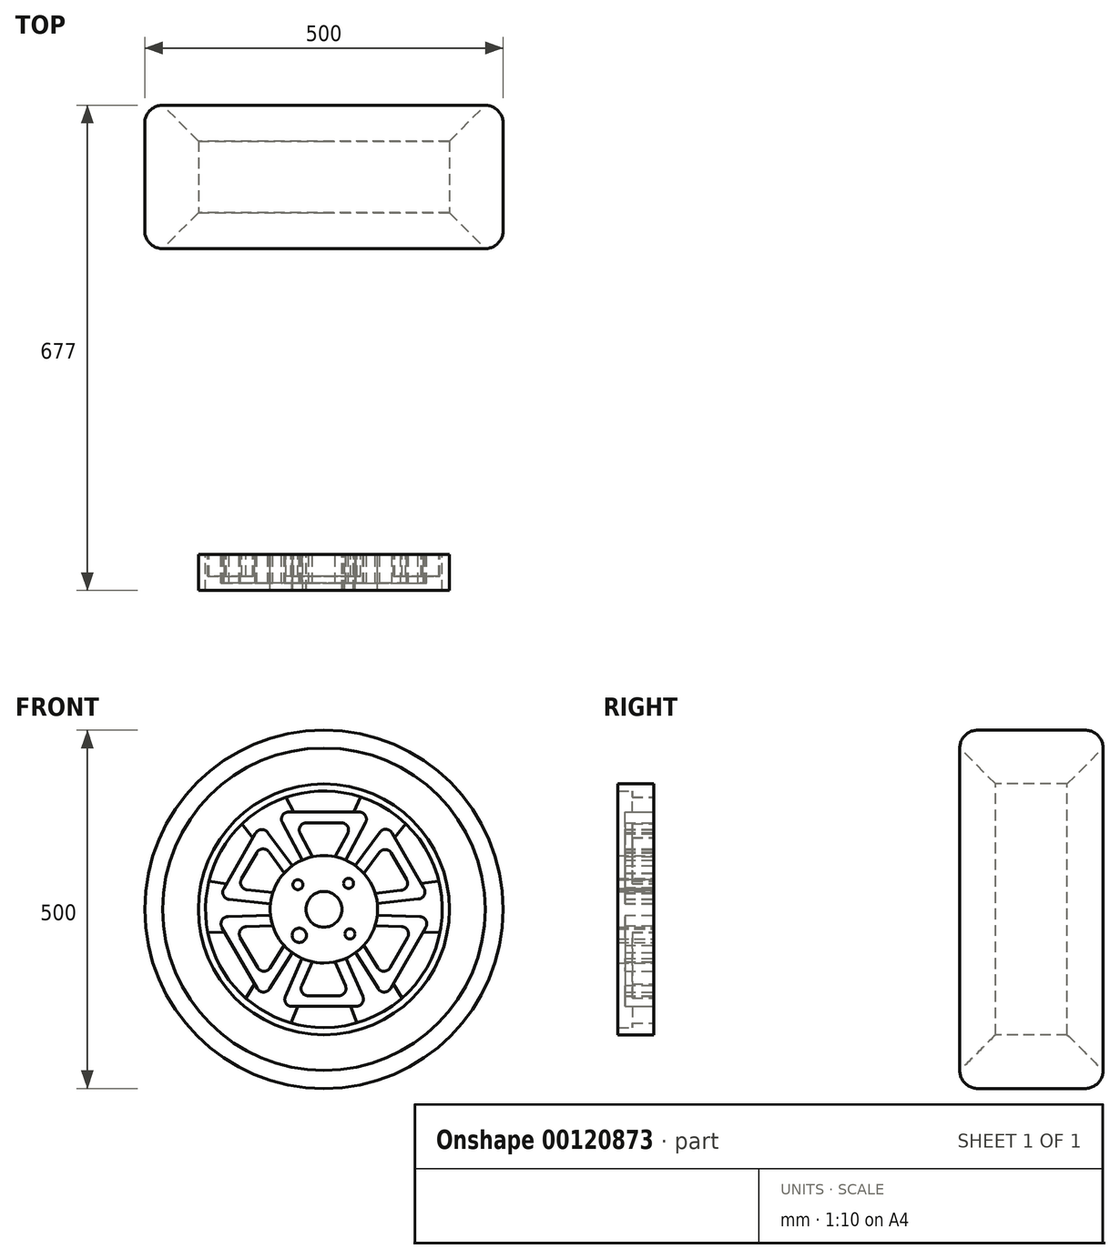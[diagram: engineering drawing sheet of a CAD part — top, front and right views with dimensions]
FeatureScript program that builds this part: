
annotation { "Feature Type Name" : "Feature", "Feature Type Description" : "" }
export const myFeature = defineFeature(function(context is Context, id is Id, definition is map)
    precondition{}
    {
        {
            var Q0;
            Q0=qCreatedBy(makeId("Front.planeOp"),FACE);
            var sketch = newSketch(context, id + "F0", { "sketchPlane" : qUnion([Q0])});
            skCircle(sketch, "E0", {"center": v(0, 0) * mm, "radius": 12.5 * mm});
            skCircle(sketch, "E1", {"center": v(0, 0) * mm, "radius": 25 * mm});
            skCircle(sketch, "E2", {"center": v(0, 0) * mm, "radius": 165.1 * mm});
            skCircle(sketch, "E3", {"center": v(0, 0) * mm, "radius": 175 * mm});
            skCircle(sketch, "E4", {"center": v(0, 0) * mm, "radius": 75 * mm});
            skLineSegment(sketch, "E5", {"start": v(0, 0) * mm, "end": v(0, 197.22) * mm, "construction": true});
            skLineSegment(sketch, "E6", {"start": v(-49.3, 135.7) * mm, "end": v(0, 135.7) * mm});
            skLineSegment(sketch, "E7.trimOffspring", {"start": v(-30.35, 68.58) * mm, "end": v(-58.13, 121.02) * mm});
            skLineSegment(sketch, "E8.MirrorCS", {"start": v(49.3, 135.7) * mm, "end": v(0, 135.7) * mm});
            skLineSegment(sketch, "E9.MirrorCS", {"start": v(30.35, 68.58) * mm, "end": v(58.13, 121.02) * mm});
            skLineSegment(sketch, "E10", {"start": v(-41.82, 135.7) * mm, "end": v(-52.8, 156.43) * mm});
            skLineSegment(sketch, "E11.MirrorCS", {"start": v(41.82, 135.7) * mm, "end": v(52.8, 156.43) * mm});
            skLineSegment(sketch, "E12.0", {"start": v(15.88, 73.3) * mm, "end": v(33.21, 106.02) * mm});
            skLineSegment(sketch, "E12.1", {"start": v(24.38, 120.7) * mm, "end": v(-1.73, 120.7) * mm});
            skLineSegment(sketch, "E12.2", {"start": v(-24.38, 120.7) * mm, "end": v(-1.73, 120.7) * mm});
            skLineSegment(sketch, "E12.3", {"start": v(-15.88, 73.3) * mm, "end": v(-33.21, 106.02) * mm});
            skPoint(sketch, "E13.visualSharp", {"position": v(-41, 120.7) * mm});
            skArc(sketch, "E13.filletArc", {"start": v(-24.38, 120.7) * mm, "mid": v(-32.94, 115.86) * mm, "end": v(-33.21, 106.02) * mm});
            skPoint(sketch, "E14.visualSharp", {"position": v(41, 120.7) * mm});
            skArc(sketch, "E14.filletArc", {"start": v(33.21, 106.02) * mm, "mid": v(32.94, 115.86) * mm, "end": v(24.38, 120.7) * mm});
            skPoint(sketch, "E15.visualSharp", {"position": v(65.91, 135.7) * mm});
            skArc(sketch, "E15.filletArc", {"start": v(58.13, 121.02) * mm, "mid": v(57.87, 130.86) * mm, "end": v(49.3, 135.7) * mm});
            skPoint(sketch, "E16.visualSharp", {"position": v(-65.91, 135.7) * mm});
            skArc(sketch, "E16.filletArc", {"start": v(-49.3, 135.7) * mm, "mid": v(-57.87, 130.86) * mm, "end": v(-58.13, 121.02) * mm});
            skLineSegment(sketch, "E17.1.0", {"start": v(-142.17, -25.16) * mm, "end": v(-117.52, -67.85) * mm});
            skLineSegment(sketch, "E17.1.1", {"start": v(-92.87, -110.54) * mm, "end": v(-117.52, -67.85) * mm});
            skArc(sketch, "E17.1.2", {"start": v(-92.87, -110.54) * mm, "mid": v(-84.4, -115.54) * mm, "end": v(-75.74, -110.86) * mm});
            skLineSegment(sketch, "E17.1.3", {"start": v(-44.22, -60.58) * mm, "end": v(-75.74, -110.86) * mm});
            skLineSegment(sketch, "E17.1.4", {"start": v(-55.54, -50.4) * mm, "end": v(-75.21, -81.77) * mm});
            skArc(sketch, "E17.1.5", {"start": v(-92.34, -81.46) * mm, "mid": v(-83.87, -86.46) * mm, "end": v(-75.21, -81.77) * mm});
            skLineSegment(sketch, "E17.1.6", {"start": v(-92.34, -81.46) * mm, "end": v(-103.67, -61.85) * mm});
            skLineSegment(sketch, "E17.1.7", {"start": v(-116.72, -39.24) * mm, "end": v(-103.67, -61.85) * mm});
            skArc(sketch, "E17.1.8", {"start": v(-108.42, -24.25) * mm, "mid": v(-116.8, -29.4) * mm, "end": v(-116.72, -39.24) * mm});
            skLineSegment(sketch, "E17.1.9", {"start": v(-71.42, -22.9) * mm, "end": v(-108.42, -24.25) * mm});
            skLineSegment(sketch, "E17.1.10", {"start": v(-74.57, -8) * mm, "end": v(-133.88, -10.17) * mm});
            skArc(sketch, "E17.1.11", {"start": v(-133.88, -10.17) * mm, "mid": v(-142.26, -15.32) * mm, "end": v(-142.17, -25.16) * mm});
            skLineSegment(sketch, "E17.2.0", {"start": v(92.87, -110.54) * mm, "end": v(117.52, -67.85) * mm});
            skLineSegment(sketch, "E17.2.1", {"start": v(142.17, -25.16) * mm, "end": v(117.52, -67.85) * mm});
            skArc(sketch, "E17.2.2", {"start": v(142.17, -25.16) * mm, "mid": v(142.26, -15.32) * mm, "end": v(133.88, -10.17) * mm});
            skLineSegment(sketch, "E17.2.3", {"start": v(74.57, -8) * mm, "end": v(133.88, -10.17) * mm});
            skLineSegment(sketch, "E17.2.4", {"start": v(71.42, -22.9) * mm, "end": v(108.42, -24.25) * mm});
            skArc(sketch, "E17.2.5", {"start": v(116.72, -39.24) * mm, "mid": v(116.8, -29.4) * mm, "end": v(108.42, -24.25) * mm});
            skLineSegment(sketch, "E17.2.6", {"start": v(116.72, -39.24) * mm, "end": v(105.4, -58.85) * mm});
            skLineSegment(sketch, "E17.2.7", {"start": v(92.34, -81.46) * mm, "end": v(105.4, -58.85) * mm});
            skArc(sketch, "E17.2.8", {"start": v(75.21, -81.77) * mm, "mid": v(83.87, -86.46) * mm, "end": v(92.34, -81.46) * mm});
            skLineSegment(sketch, "E17.2.9", {"start": v(55.54, -50.4) * mm, "end": v(75.21, -81.77) * mm});
            skLineSegment(sketch, "E17.2.10", {"start": v(44.22, -60.58) * mm, "end": v(75.74, -110.86) * mm});
            skArc(sketch, "E17.2.11", {"start": v(75.74, -110.86) * mm, "mid": v(84.4, -115.54) * mm, "end": v(92.87, -110.54) * mm});
            skLineSegment(sketch, "E18.1.0", {"start": v(138.43, -31.64) * mm, "end": v(161.87, -32.5) * mm});
            skLineSegment(sketch, "E18.1.1", {"start": v(96.61, -104.07) * mm, "end": v(109.07, -123.94) * mm});
            skLineSegment(sketch, "E18.2.0", {"start": v(-96.61, -104.07) * mm, "end": v(-109.07, -123.94) * mm});
            skLineSegment(sketch, "E18.2.1", {"start": v(-138.43, -31.64) * mm, "end": v(-161.87, -32.5) * mm});
            skLineSegment(sketch, "E19.MirrorCS", {"start": v(95.06, 106.32) * mm, "end": v(116.88, 68.53) * mm});
            skLineSegment(sketch, "E20.MirrorCS", {"start": v(94.06, 78.37) * mm, "end": v(104.71, 59.92) * mm});
            skLineSegment(sketch, "E21.MirrorCS", {"start": v(55.86, 50.05) * mm, "end": v(77.34, 79.3) * mm});
            skLineSegment(sketch, "E22.MirrorCS", {"start": v(43.77, 60.9) * mm, "end": v(78.05, 107.56) * mm});
            skArc(sketch, "E23.MirrorCS", {"start": v(77.34, 79.3) * mm, "mid": v(85.95, 83.36) * mm, "end": v(94.06, 78.37) * mm});
            skArc(sketch, "E24.MirrorCS", {"start": v(78.05, 107.56) * mm, "mid": v(86.9, 111.7) * mm, "end": v(95.06, 106.32) * mm});
            skLineSegment(sketch, "E25.MirrorCS", {"start": v(138.88, 30.41) * mm, "end": v(116.88, 68.53) * mm});
            skLineSegment(sketch, "E26.MirrorCS", {"start": v(115.14, 41.86) * mm, "end": v(104.71, 59.92) * mm});
            skArc(sketch, "E27.MirrorCS", {"start": v(107.28, 26.4) * mm, "mid": v(115.68, 31.85) * mm, "end": v(115.14, 41.86) * mm});
            skLineSegment(sketch, "E28.MirrorCS", {"start": v(71.56, 22.46) * mm, "end": v(107.28, 26.4) * mm});
            skLineSegment(sketch, "E29.MirrorCS", {"start": v(74.58, 7.95) * mm, "end": v(131.54, 14.24) * mm});
            skArc(sketch, "E30.MirrorCS", {"start": v(131.54, 14.24) * mm, "mid": v(140.13, 20.1) * mm, "end": v(138.88, 30.41) * mm});
            skLineSegment(sketch, "E31.MirrorCS", {"start": v(41.82, 135.7) * mm, "end": v(51.15, 156.98) * mm});
            skLineSegment(sketch, "E32", {"start": v(98.57, 100.23) * mm, "end": v(114.27, 119.17) * mm});
            skLineSegment(sketch, "E33.MirrorCS", {"start": v(135.6, 36.1) * mm, "end": v(160.3, 39.5) * mm});
            skLineSegment(sketch, "E34.1.0", {"start": v(-74.63, 7.46) * mm, "end": v(-132.17, 13.81) * mm});
            skLineSegment(sketch, "E34.1.1", {"start": v(-71.27, 23.35) * mm, "end": v(-107.34, 27.33) * mm});
            skArc(sketch, "E34.1.2", {"start": v(-107.34, 27.33) * mm, "mid": v(-115.16, 32.75) * mm, "end": v(-114.9, 42.27) * mm});
            skArc(sketch, "E34.1.3", {"start": v(-132.17, 13.81) * mm, "mid": v(-140.19, 19.4) * mm, "end": v(-139.6, 29.16) * mm});
            skLineSegment(sketch, "E34.1.4", {"start": v(-136.09, 35.25) * mm, "end": v(-160.34, 39.38) * mm});
            skLineSegment(sketch, "E34.1.5", {"start": v(-139.6, 29.16) * mm, "end": v(-117.78, 66.95) * mm});
            skLineSegment(sketch, "E34.1.6", {"start": v(-114.9, 42.27) * mm, "end": v(-104.25, 60.73) * mm});
            skLineSegment(sketch, "E34.1.7", {"start": v(-93.82, 78.79) * mm, "end": v(-104.25, 60.73) * mm});
            skArc(sketch, "E34.1.8", {"start": v(-76.5, 79.7) * mm, "mid": v(-85.43, 84.25) * mm, "end": v(-93.82, 78.79) * mm});
            skLineSegment(sketch, "E34.1.9", {"start": v(-55.23, 50.74) * mm, "end": v(-76.5, 79.7) * mm});
            skLineSegment(sketch, "E34.1.10", {"start": v(-95.78, 105.07) * mm, "end": v(-117.78, 66.95) * mm});
            skLineSegment(sketch, "E34.1.11", {"start": v(-44.17, 60.61) * mm, "end": v(-78.1, 106.8) * mm});
            skArc(sketch, "E34.1.12", {"start": v(-78.1, 106.8) * mm, "mid": v(-87.47, 111.31) * mm, "end": v(-95.78, 105.07) * mm});
            skLineSegment(sketch, "E34.1.13", {"start": v(-99.06, 99.39) * mm, "end": v(-114.35, 119.09) * mm});
            skLineSegment(sketch, "E34.2.0", {"start": v(30.86, -68.36) * mm, "end": v(54.12, -121.37) * mm});
            skLineSegment(sketch, "E34.2.1", {"start": v(15.42, -73.4) * mm, "end": v(30, -106.62) * mm});
            skArc(sketch, "E34.2.2", {"start": v(30, -106.62) * mm, "mid": v(29.22, -116.11) * mm, "end": v(20.84, -120.64) * mm});
            skArc(sketch, "E34.2.3", {"start": v(54.12, -121.37) * mm, "mid": v(53.29, -131.1) * mm, "end": v(44.55, -135.48) * mm});
            skLineSegment(sketch, "E34.2.4", {"start": v(37.51, -135.48) * mm, "end": v(46.07, -158.54) * mm});
            skLineSegment(sketch, "E34.2.5", {"start": v(44.55, -135.48) * mm, "end": v(0.9, -135.48) * mm});
            skLineSegment(sketch, "E34.2.6", {"start": v(20.84, -120.64) * mm, "end": v(-0.47, -120.64) * mm});
            skLineSegment(sketch, "E34.2.7", {"start": v(-21.32, -120.64) * mm, "end": v(-0.47, -120.64) * mm});
            skArc(sketch, "E34.2.8", {"start": v(-30.77, -106.1) * mm, "mid": v(-30.25, -116.1) * mm, "end": v(-21.32, -120.64) * mm});
            skLineSegment(sketch, "E34.2.9", {"start": v(-16.33, -73.2) * mm, "end": v(-30.77, -106.1) * mm});
            skLineSegment(sketch, "E34.2.10", {"start": v(-43.1, -135.48) * mm, "end": v(0.9, -135.48) * mm});
            skLineSegment(sketch, "E34.2.11", {"start": v(-30.4, -68.56) * mm, "end": v(-53.44, -121.04) * mm});
            skArc(sketch, "E34.2.12", {"start": v(-53.44, -121.04) * mm, "mid": v(-52.67, -131.4) * mm, "end": v(-43.1, -135.48) * mm});
            skLineSegment(sketch, "E34.2.13", {"start": v(-36.54, -135.48) * mm, "end": v(-45.95, -158.58) * mm});
            skCircle(sketch, "E35", {"center": v(-36.27, 34.36) * mm, "radius": 7 * mm});
            skCircle(sketch, "E36", {"center": v(-36.27, 34.36) * mm, "radius": 10 * mm});
            skCircle(sketch, "E37", {"center": v(36.27, -34.36) * mm, "radius": 10 * mm});
            skCircle(sketch, "E38", {"center": v(36.27, -34.36) * mm, "radius": 7 * mm});
            skCircle(sketch, "E39", {"center": v(34.36, 36.27) * mm, "radius": 7 * mm});
            skCircle(sketch, "E40", {"center": v(34.36, 36.27) * mm, "radius": 10 * mm});
            skCircle(sketch, "E41.MirrorC", {"center": v(-34.36, -36.27) * mm, "radius": 10 * mm});
            skCircle(sketch, "E42.MirrorC", {"center": v(-34.36, -36.27) * mm, "radius": 7 * mm});
            skCircle(sketch, "E43", {"center": v(0, 0) * mm, "radius": 250 * mm});
            skSolve(sketch);
        }
        {
            var Q0;
            Q0=makeQuery(id+"F0.imprint","IMPRINT",FACE,{"disambiguationData":[TD([[makeQuery(id+"F0.imprint","IMPRINT",EDGE,{"derivedFrom":sQuery(id+"F0.wireOp",EDGE,"E1")}),-1.0]])]});
            var Q1;
            Q1=makeQuery(id+"F0.imprint","IMPRINT",FACE,{"disambiguationData":[TD([[makeQuery(id+"F0.imprint","IMPRINT",EDGE,{"derivedFrom":sQuery(id+"F0.wireOp",EDGE,"E35")}),-1.0]])]});
            var Q2;
            Q2=makeQuery(id+"F0.imprint","IMPRINT",FACE,{"disambiguationData":[TD([[makeQuery(id+"F0.imprint","IMPRINT",EDGE,{"derivedFrom":sQuery(id+"F0.wireOp",EDGE,"E41.MirrorC")}),-1.0]])]});
            var Q3;
            Q3=makeQuery(id+"F0.imprint","IMPRINT",FACE,{"disambiguationData":[TD([[makeQuery(id+"F0.imprint","IMPRINT",EDGE,{"derivedFrom":sQuery(id+"F0.wireOp",EDGE,"E37")}),1.0]])]});
            var Q4;
            Q4=makeQuery(id+"F0.imprint","IMPRINT",FACE,{"disambiguationData":[TD([[makeQuery(id+"F0.imprint","IMPRINT",EDGE,{"derivedFrom":sQuery(id+"F0.wireOp",EDGE,"E39")}),-1.0]])]});
            extrude(context, id + "F1", {"entities" : qUnion([Q0, Q1, Q2, Q3, Q4]), "depth" : 50 * mm});
        }
        {
            var Q0;
            {var subQ0=sQuery(id+"F0.wireOp",EDGE,"E7.trimOffspring");Q0=makeQuery(id+"F0.imprint","IMPRINT",FACE,{"disambiguationData":[TD([[makeQuery(id+"F0.imprint","IMPRINT",EDGE,{"derivedFrom":subQ0}),-1.0]])]});}
            var Q1;
            Q1=makeQuery(id+"F0.imprint","IMPRINT",FACE,{"disambiguationData":[TD([[makeQuery(id+"F0.imprint","IMPRINT",EDGE,{"derivedFrom":sQuery(id+"F0.wireOp",EDGE,"E20.MirrorCS")}),1.0]])]});
            var Q2;
            {var subQ10=sQuery(id+"F0.wireOp",EDGE,"E17.2.2");Q2=makeQuery(id+"F0.imprint","IMPRINT",FACE,{"disambiguationData":[TD([[makeQuery(id+"F0.imprint","IMPRINT",EDGE,{"derivedFrom":subQ10}),1.0]])]});}
            var Q3;
            {var subQ10=sQuery(id+"F0.wireOp",EDGE,"E34.2.0");Q3=makeQuery(id+"F0.imprint","IMPRINT",FACE,{"disambiguationData":[TD([[makeQuery(id+"F0.imprint","IMPRINT",EDGE,{"derivedFrom":subQ10}),-1.0]])]});}
            var Q4;
            {var subQ5=sQuery(id+"F0.wireOp",EDGE,"E17.1.2");Q4=makeQuery(id+"F0.imprint","IMPRINT",FACE,{"disambiguationData":[TD([[makeQuery(id+"F0.imprint","IMPRINT",EDGE,{"derivedFrom":subQ5}),1.0]])]});}
            var Q5;
            {var subQ5=sQuery(id+"F0.wireOp",EDGE,"E34.1.0");Q5=makeQuery(id+"F0.imprint","IMPRINT",FACE,{"disambiguationData":[TD([[makeQuery(id+"F0.imprint","IMPRINT",EDGE,{"derivedFrom":subQ5}),-1.0]])]});}
            extrude(context, id + "F2", {"entities" : qUnion([Q0, Q1, Q2, Q3, Q4, Q5]), "operationType" : NewBodyOperationType.ADD, "depth" : 40 * mm});
        }
        {
            var Q0;
            {var subQ0=sQuery(id+"F0.wireOp",EDGE,"E10");Q0=makeQuery(id+"F0.imprint","IMPRINT",FACE,{"disambiguationData":[TD([[makeQuery(id+"F0.imprint","IMPRINT",EDGE,{"derivedFrom":subQ0}),-1.0]])]});}
            var Q1;
            {var subQ0=sQuery(id+"F0.wireOp",EDGE,"E32");Q1=makeQuery(id+"F0.imprint","IMPRINT",FACE,{"disambiguationData":[TD([[makeQuery(id+"F0.imprint","IMPRINT",EDGE,{"derivedFrom":subQ0}),-1.0]])]});}
            var Q2;
            {var subQ0=sQuery(id+"F0.wireOp",EDGE,"E18.1.0");Q2=makeQuery(id+"F0.imprint","IMPRINT",FACE,{"disambiguationData":[TD([[makeQuery(id+"F0.imprint","IMPRINT",EDGE,{"derivedFrom":subQ0}),-1.0]])]});}
            var Q3;
            {var subQ4=sQuery(id+"F0.wireOp",EDGE,"E34.2.4");Q3=makeQuery(id+"F0.imprint","IMPRINT",FACE,{"disambiguationData":[TD([[makeQuery(id+"F0.imprint","IMPRINT",EDGE,{"derivedFrom":subQ4}),-1.0]])]});}
            var Q4;
            {var subQ0=sQuery(id+"F0.wireOp",EDGE,"E18.2.0");Q4=makeQuery(id+"F0.imprint","IMPRINT",FACE,{"disambiguationData":[TD([[makeQuery(id+"F0.imprint","IMPRINT",EDGE,{"derivedFrom":subQ0}),-1.0]])]});}
            var Q5;
            {var subQ1=sQuery(id+"F0.wireOp",EDGE,"E34.1.4");Q5=makeQuery(id+"F0.imprint","IMPRINT",FACE,{"disambiguationData":[TD([[makeQuery(id+"F0.imprint","IMPRINT",EDGE,{"derivedFrom":subQ1}),-1.0]])]});}
            extrude(context, id + "F3", {"entities" : qUnion([Q0, Q1, Q2, Q3, Q4, Q5]), "operationType" : NewBodyOperationType.ADD, "depth" : 30 * mm});
        }
        {
            var Q0;
            Q0=makeQuery(id+"F0.imprint","IMPRINT",FACE,{"disambiguationData":[TD([[makeQuery(id+"F0.imprint","IMPRINT",EDGE,{"derivedFrom":sQuery(id+"F0.wireOp",EDGE,"E3")}),1.0]])]});
            extrude(context, id + "F4", {"entities" : qUnion([Q0]), "operationType" : NewBodyOperationType.ADD, "depth" : 50 * mm});
        }
        {
            var Q0;
            Q0=makeQuery(id+"F0.imprint","IMPRINT",FACE,{"disambiguationData":[TD([[makeQuery(id+"F0.imprint","IMPRINT",EDGE,{"derivedFrom":sQuery(id+"F0.wireOp",EDGE,"E3")}),-1.0]])]});
            extrude(context, id + "F5", {"entities" : qUnion([Q0]), "oppositeDirection" : true, "depth" : 200 * mm});
        }
        {
            var Q0;
            Q0=makeQuery(id+"F5.opExtrude","CAP_EDGE",EDGE,{"disambiguationData":[OSD([sQuery(id+"F0.wireOp",EDGE,"E43")])],"isStart":false});
            var Q1;
            Q1=makeQuery(id+"F5.opExtrude","CAP_EDGE",EDGE,{"disambiguationData":[OSD([sQuery(id+"F0.wireOp",EDGE,"E43")])],"isStart":true});
            fillet(context, id + "F6", {"entities" : qUnion([Q0, Q1]), "radius" : 25 * mm, "tangentPropagation" : true, "allowEdgeOverflow" : false});
        }
        {
            var Q0;
            Q0=makeQuery(id+"F5.opExtrude","SWEPT_BODY",BODY,{"disambiguationData":[OSD([sQuery(id+"F0.wireOp",EDGE,"E3"),sQuery(id+"F0.wireOp",EDGE,"E43")])]});
            transform(context, id + "F7", {"entities" : qUnion([Q0]), "transformType" : TransformType.TRANSLATION_3D, "dx" : 0 * mm, "dy" : 427 * mm, "dz" : 0 * mm, "makeCopy" : false});
        }
        {
            var Q0;
            Q0=makeQuery(id+"F5.opExtrude","CAP_EDGE",EDGE,{"disambiguationData":[OSD([sQuery(id+"F0.wireOp",EDGE,"E3")])],"isStart":true});
            var Q1;
            Q1=makeQuery(id+"F5.opExtrude","CAP_EDGE",EDGE,{"disambiguationData":[OSD([sQuery(id+"F0.wireOp",EDGE,"E3")])],"isStart":false});
            chamfer(context, id + "F8", {"entities" : qUnion([Q0, Q1]), "width" : 50 * mm, "tangentPropagation" : true});
        }
    });
